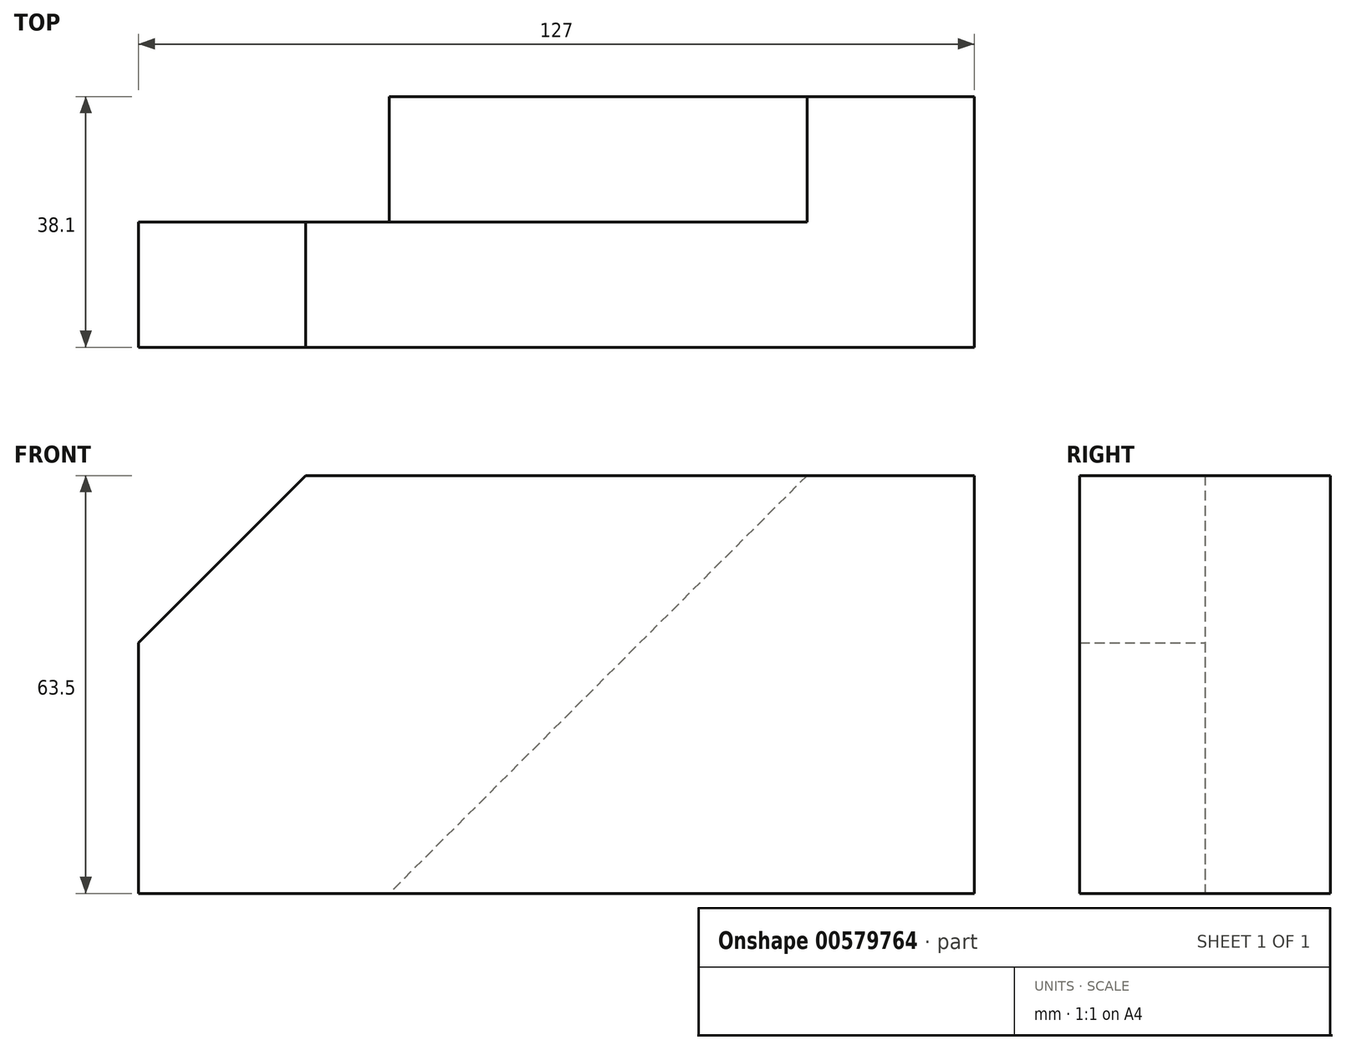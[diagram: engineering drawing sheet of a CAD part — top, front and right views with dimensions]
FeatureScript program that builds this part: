
annotation { "Feature Type Name" : "Feature", "Feature Type Description" : "" }
export const myFeature = defineFeature(function(context is Context, id is Id, definition is map)
    precondition{}
    {
        {
            var Q0;
            Q0=qCreatedBy(makeId("Front.planeOp"),FACE);
            var sketch = newSketch(context, id + "F0", { "sketchPlane" : qUnion([Q0])});
            skLineSegment(sketch, "E0.bottom", {"start": v(-57.85, 12.56) * mm, "end": v(69.15, 12.56) * mm});
            skLineSegment(sketch, "E0.top", {"start": v(-57.85, -50.94) * mm, "end": v(69.15, -50.94) * mm});
            skLineSegment(sketch, "E0.left", {"start": v(-57.85, 12.56) * mm, "end": v(-57.85, -50.94) * mm});
            skLineSegment(sketch, "E0.right", {"start": v(69.15, 12.56) * mm, "end": v(69.15, -50.94) * mm});
            skSolve(sketch);
        }
        {
            var Q0;
            Q0=makeQuery(id+"F0.imprint","IMPRINT",FACE,{"disambiguationData":[TD([[makeQuery(id+"F0.imprint","IMPRINT",EDGE,{"derivedFrom":sQuery(id+"F0.wireOp",EDGE,"E0.bottom")}),-1.0]])]});
            extrude(context, id + "F1", {"entities" : qUnion([Q0]), "depth" : 38.1 * mm, "offsetDistance" : 25.4 * mm});
        }
        {
            var Q0;
            Q0=qCreatedBy(makeId("Front.planeOp"),FACE);
            var sketch = newSketch(context, id + "F2", { "sketchPlane" : qUnion([Q0])});
            skLineSegment(sketch, "E1", {"start": v(-32.45, 12.56) * mm, "end": v(-57.85, -12.84) * mm});
            skLineSegment(sketch, "E2", {"start": v(-32.45, 12.56) * mm, "end": v(-62, 12.56) * mm});
            skLineSegment(sketch, "E3", {"start": v(-62, 12.56) * mm, "end": v(-62, -12.83) * mm});
            skLineSegment(sketch, "E4", {"start": v(-62, -12.83) * mm, "end": v(-57.85, -12.84) * mm});
            skSolve(sketch);
        }
        {
            var Q0;
            Q0=makeQuery(id+"F2.imprint","IMPRINT",FACE,{"disambiguationData":[TD([[makeQuery(id+"F2.imprint","IMPRINT",EDGE,{"derivedFrom":sQuery(id+"F2.wireOp",EDGE,"E1")}),-1.0]])]});
            extrude(context, id + "F3", {"entities" : qUnion([Q0]), "operationType" : NewBodyOperationType.REMOVE, "depth" : 50.8 * mm, "offsetDistance" : 25.4 * mm});
        }
        {
            var Q0;
            Q0=qCreatedBy(makeId("Front.planeOp"),FACE);
            var sketch = newSketch(context, id + "F4", { "sketchPlane" : qUnion([Q0])});
            skLineSegment(sketch, "E5", {"start": v(43.75, 12.56) * mm, "end": v(-19.75, -50.94) * mm});
            skLineSegment(sketch, "E6", {"start": v(43.75, 12.56) * mm, "end": v(-59.24, 12.56) * mm});
            skLineSegment(sketch, "E7", {"start": v(-59.24, 12.56) * mm, "end": v(-59.24, -51) * mm});
            skLineSegment(sketch, "E8", {"start": v(-59.24, -51) * mm, "end": v(-19.75, -50.94) * mm});
            skSolve(sketch);
        }
        {
            var Q0;
            Q0=qSketchRegion(id+"F4",true);
            extrude(context, id + "F5", {"entities" : qUnion([Q0]), "operationType" : NewBodyOperationType.REMOVE, "depth" : 19.05 * mm, "offsetDistance" : 25.4 * mm});
        }
    });
